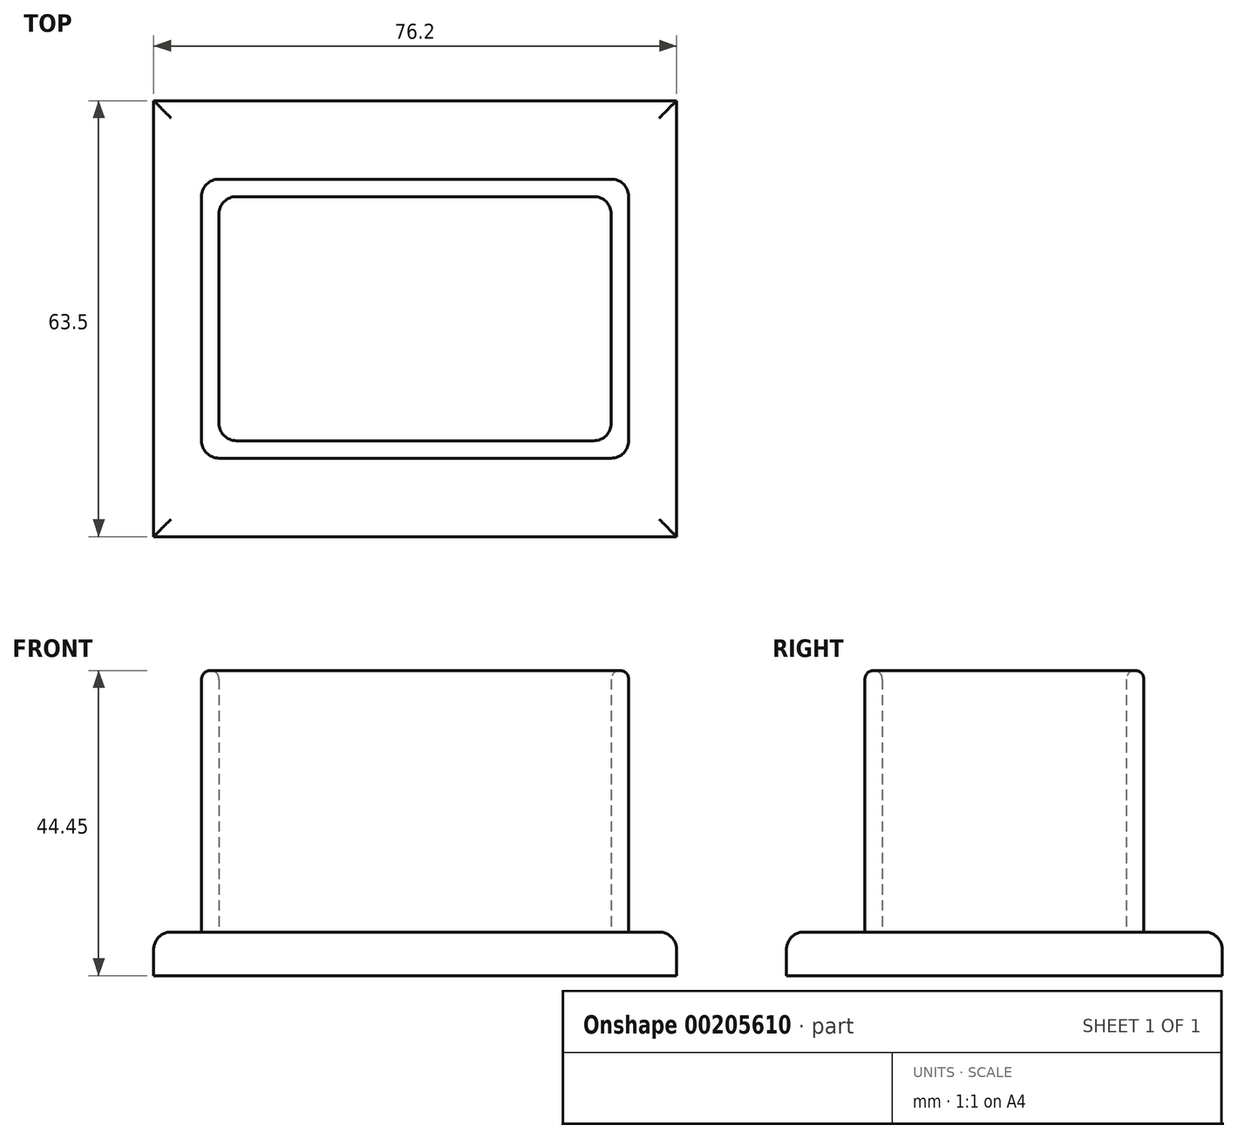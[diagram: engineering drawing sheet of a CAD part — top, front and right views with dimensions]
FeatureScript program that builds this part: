
annotation { "Feature Type Name" : "Feature", "Feature Type Description" : "" }
export const myFeature = defineFeature(function(context is Context, id is Id, definition is map)
    precondition{}
    {
        {
            var Q0;
            Q0=qCreatedBy(makeId("Top.planeOp"),FACE);
            var sketch = newSketch(context, id + "F0", { "sketchPlane" : qUnion([Q0])});
            skLineSegment(sketch, "E0.bottom", {"start": v(38.1, -31.75) * mm, "end": v(-38.1, -31.75) * mm});
            skLineSegment(sketch, "E0.top", {"start": v(38.1, 31.75) * mm, "end": v(-38.1, 31.75) * mm});
            skLineSegment(sketch, "E0.left", {"start": v(38.1, -31.75) * mm, "end": v(38.1, 31.75) * mm});
            skLineSegment(sketch, "E0.right", {"start": v(-38.1, -31.75) * mm, "end": v(-38.1, 31.75) * mm});
            skPoint(sketch, "E0.middle", {"position": v(0, 0) * mm});
            skSolve(sketch);
        }
        {
            var Q0;
            Q0=makeQuery(id+"F0.imprint","IMPRINT",FACE,{"disambiguationData":[TD([[makeQuery(id+"F0.imprint","IMPRINT",EDGE,{"derivedFrom":sQuery(id+"F0.wireOp",EDGE,"E0.bottom")}),-1.0]])]});
            extrude(context, id + "F1", {"entities" : qUnion([Q0]), "depth" : 6.35 * mm});
        }
        {
            var Q0;
            Q0=makeQuery(id+"F1.opExtrude","CAP_FACE",FACE,{"disambiguationData":[OSD([sQuery(id+"F0.wireOp",EDGE,"E0.bottom"),sQuery(id+"F0.wireOp",EDGE,"E0.top"),sQuery(id+"F0.wireOp",EDGE,"E0.left"),sQuery(id+"F0.wireOp",EDGE,"E0.right")])],"isStart":false});
            var sketch = newSketch(context, id + "F2", { "sketchPlane" : qUnion([Q0])});
            skLineSegment(sketch, "E1.bottom", {"start": v(31.12, -20.32) * mm, "end": v(-31.12, -20.32) * mm});
            skLineSegment(sketch, "E1.top", {"start": v(31.12, 20.32) * mm, "end": v(-31.12, 20.32) * mm});
            skLineSegment(sketch, "E1.left", {"start": v(31.12, -20.32) * mm, "end": v(31.12, 20.32) * mm});
            skLineSegment(sketch, "E1.right", {"start": v(-31.12, -20.32) * mm, "end": v(-31.12, 20.32) * mm});
            skPoint(sketch, "E1.middle", {"position": v(0, 0) * mm});
            skLineSegment(sketch, "E2.bottom", {"start": v(28.58, -17.78) * mm, "end": v(-28.58, -17.78) * mm});
            skLineSegment(sketch, "E2.top", {"start": v(28.58, 17.78) * mm, "end": v(-28.58, 17.78) * mm});
            skLineSegment(sketch, "E2.left", {"start": v(28.58, -17.78) * mm, "end": v(28.58, 17.78) * mm});
            skLineSegment(sketch, "E2.right", {"start": v(-28.58, -17.78) * mm, "end": v(-28.58, 17.78) * mm});
            skSolve(sketch);
        }
        {
            var Q0;
            Q0=makeQuery(id+"F2.imprint","IMPRINT",FACE,{"disambiguationData":[TD([[makeQuery(id+"F2.imprint","IMPRINT",EDGE,{"derivedFrom":sQuery(id+"F2.wireOp",EDGE,"E1.bottom")}),-1.0]])]});
            extrude(context, id + "F3", {"entities" : qUnion([Q0]), "operationType" : NewBodyOperationType.ADD, "depth" : 38.1 * mm});
        }
        {
            var Q0;
            Q0=makeQuery(id+"F3.opExtrude","SWEPT_EDGE",EDGE,{"disambiguationData":[OSD([sQuery(id+"F2.wireOp",EDGE,"E2.top"),sQuery(id+"F2.wireOp",EDGE,"E2.right")])]});
            var Q1;
            Q1=makeQuery(id+"F3.opExtrude","SWEPT_EDGE",EDGE,{"disambiguationData":[OSD([sQuery(id+"F2.wireOp",EDGE,"E2.bottom"),sQuery(id+"F2.wireOp",EDGE,"E2.right")])]});
            var Q2;
            Q2=makeQuery(id+"F3.opExtrude","SWEPT_EDGE",EDGE,{"disambiguationData":[OSD([sQuery(id+"F2.wireOp",EDGE,"E2.top"),sQuery(id+"F2.wireOp",EDGE,"E2.left")])]});
            var Q3;
            Q3=makeQuery(id+"F3.opExtrude","SWEPT_EDGE",EDGE,{"disambiguationData":[OSD([sQuery(id+"F2.wireOp",EDGE,"E2.bottom"),sQuery(id+"F2.wireOp",EDGE,"E2.left")])]});
            var Q4;
            Q4=makeQuery(id+"F3.opExtrude","CAP_EDGE",EDGE,{"disambiguationData":[OSD([sQuery(id+"F2.wireOp",EDGE,"E1.bottom")])],"isStart":true});
            var Q5;
            Q5=makeQuery(id+"F3.opExtrude","CAP_EDGE",EDGE,{"disambiguationData":[OSD([sQuery(id+"F2.wireOp",EDGE,"E1.left")])],"isStart":true});
            var Q6;
            Q6=makeQuery(id+"F3.opExtrude","CAP_EDGE",EDGE,{"disambiguationData":[OSD([sQuery(id+"F2.wireOp",EDGE,"E1.right")])],"isStart":true});
            var Q7;
            Q7=makeQuery(id+"F3.opExtrude","CAP_EDGE",EDGE,{"disambiguationData":[OSD([sQuery(id+"F2.wireOp",EDGE,"E1.top")])],"isStart":true});
            var Q8;
            Q8=makeQuery(id+"F1.opExtrude","CAP_EDGE",EDGE,{"disambiguationData":[OSD([sQuery(id+"F0.wireOp",EDGE,"E0.top")])],"isStart":false});
            var Q9;
            Q9=makeQuery(id+"F1.opExtrude","CAP_EDGE",EDGE,{"disambiguationData":[OSD([sQuery(id+"F0.wireOp",EDGE,"E0.right")])],"isStart":false});
            var Q10;
            Q10=makeQuery(id+"F1.opExtrude","CAP_EDGE",EDGE,{"disambiguationData":[OSD([sQuery(id+"F0.wireOp",EDGE,"E0.bottom")])],"isStart":false});
            var Q11;
            Q11=makeQuery(id+"F1.opExtrude","CAP_EDGE",EDGE,{"disambiguationData":[OSD([sQuery(id+"F0.wireOp",EDGE,"E0.left")])],"isStart":false});
            var Q12;
            Q12=makeQuery(id+"F3.opExtrude","SWEPT_EDGE",EDGE,{"disambiguationData":[OSD([sQuery(id+"F2.wireOp",EDGE,"E1.bottom"),sQuery(id+"F2.wireOp",EDGE,"E1.right")])]});
            var Q13;
            Q13=makeQuery(id+"F3.opExtrude","SWEPT_EDGE",EDGE,{"disambiguationData":[OSD([sQuery(id+"F2.wireOp",EDGE,"E1.top"),sQuery(id+"F2.wireOp",EDGE,"E1.right")])]});
            var Q14;
            Q14=makeQuery(id+"F3.opExtrude","SWEPT_EDGE",EDGE,{"disambiguationData":[OSD([sQuery(id+"F2.wireOp",EDGE,"E1.bottom"),sQuery(id+"F2.wireOp",EDGE,"E1.left")])]});
            var Q15;
            Q15=makeQuery(id+"F3.opExtrude","SWEPT_EDGE",EDGE,{"disambiguationData":[OSD([sQuery(id+"F2.wireOp",EDGE,"E1.top"),sQuery(id+"F2.wireOp",EDGE,"E1.left")])]});
            fillet(context, id + "F4", {"entities" : qUnion([Q0, Q1, Q2, Q3, Q4, Q5, Q6, Q7, Q8, Q9, Q10, Q11, Q12, Q13, Q14, Q15]), "radius" : 2.54 * mm, "tangentPropagation" : true, "allowEdgeOverflow" : false});
        }
        {
            var Q0;
            Q0=makeQuery(id+"F3.opExtrude","CAP_FACE",FACE,{"disambiguationData":[OSD([sQuery(id+"F2.wireOp",EDGE,"E1.bottom"),sQuery(id+"F2.wireOp",EDGE,"E1.top"),sQuery(id+"F2.wireOp",EDGE,"E1.left"),sQuery(id+"F2.wireOp",EDGE,"E1.right"),sQuery(id+"F2.wireOp",EDGE,"E2.bottom"),sQuery(id+"F2.wireOp",EDGE,"E2.top"),sQuery(id+"F2.wireOp",EDGE,"E2.left"),sQuery(id+"F2.wireOp",EDGE,"E2.right")])],"isStart":false});
            fillet(context, id + "F5", {"entities" : qUnion([Q0]), "radius" : 1.27 * mm, "tangentPropagation" : true, "allowEdgeOverflow" : false});
        }
    });
